# Revit family: 0047930 Sylvania Lighting Fixture START eco Bollard Rectangular M IP65 780lm 830 BLK
name_source: partatom
category: Lighting Fixtures
revit_build: Autodesk Revit 2016 (Build: 20150220_1215(x64)
units: mm (PartAtom-declared; Revit-internal decimal feet)

## family parameters
Cut with Voids When Loaded = No
Host = Face
Light Source = Yes
OmniClass Number = 23.80.70.00
OmniClass Title = Lighting
Part Type = Normal
Room Calculation Point = No
Round Connector Dimension = Use Diameter
Shared = No

## types (1)
- 0047930 ST E BLLRD RECT M IP65 780LM 830 BLK
    Apparent Load = 12 VA
    Assembly Code = D5020200
    AssetType = Fixed
    ClassificationName = Uniclass2015
    ClassificationValue = EF_70_80
    Color Filter = 16777215
    Cost = 0 $
    Default Elevation = 1219 mm
    Dimming Lamp Color Temperature Shift = <None>
    DimmingControlOptions = Non dimmable
    DocumentationLiterature = http://www.sylvania-lighting.com
    DurationUnit = hours
    ElectricShockClassification = Class I
    Emit Shape Visible in Rendering = No
    Emit from Rectangle Length = 16 mm  [stored 0.0524934 ft]
    Emit from Rectangle Width = 150 mm
    ExpectedLife = 50000
    Height_SYL = 500 mm
    IfcExportAs = IfcLightFixtureType
    IfcExportType = IfcLightFixtureType
    ImpactProtectionIndex = IK10
    IngressProtection = IP65
    InputNominalFrequency = 50/60 Hz
    InputVoltage = 220-240V~
    Keynote = 16500
    Lamp = LED
    LampColourRenderingIndex = 80
    LampColourTemperature = 3000
    LampNominalLuminous = 524 lm
    LampsType = LED
    LightOutputRatio = 100
    LuminousEfficacy = 44 lm/W
    Manufacturer = Feilo Sylvania
    ManufacturerName = Feilo Sylvania
    Material_1_SYL = Steel, Paint Finish, Dark Gray, Matte
    Material_2_SYL = LED-Sylvania-STARTBollardRect
    Material_3_SYL = <By Category>
    Material_4_SYL = <By Category>
    Model = START eco Bollard Rectangular M IP65 780lm 830 BLK
    ModelNumber = 0047930
    ModelReference = START eco Bollard Rectangular M IP65 780lm 830 BLK
    Name = START eco Bollard Rectangular M IP65 780lm 830 BLK
    NominalDepth = 80 mm  [stored 0.262467 ft]
    NominalHeight = 500 mm
    NominalLength = 190 mm
    Photometric Web File = 0047930.ies
    PowerConsumption = 12 W
    PowerFactor = 0
    RadiusReflector_SYL = 13 mm
    Tilt Angle = 90.00°
    Type Image = <None>
    TypeName = START eco Bollard Rectangular M IP65 780lm 830 BLK
    URL = http://www.sylvania-lighting.com
    Voltage = 230 V
    Weight = 6.08 kg

note: [stored X ft] marks values corroborated as IEEE doubles in the binary element streams (Revit-internal decimal feet)

## geometry (parser evidence)
native form markers: Sweep x2
no freeform markers — native parametric forms only
